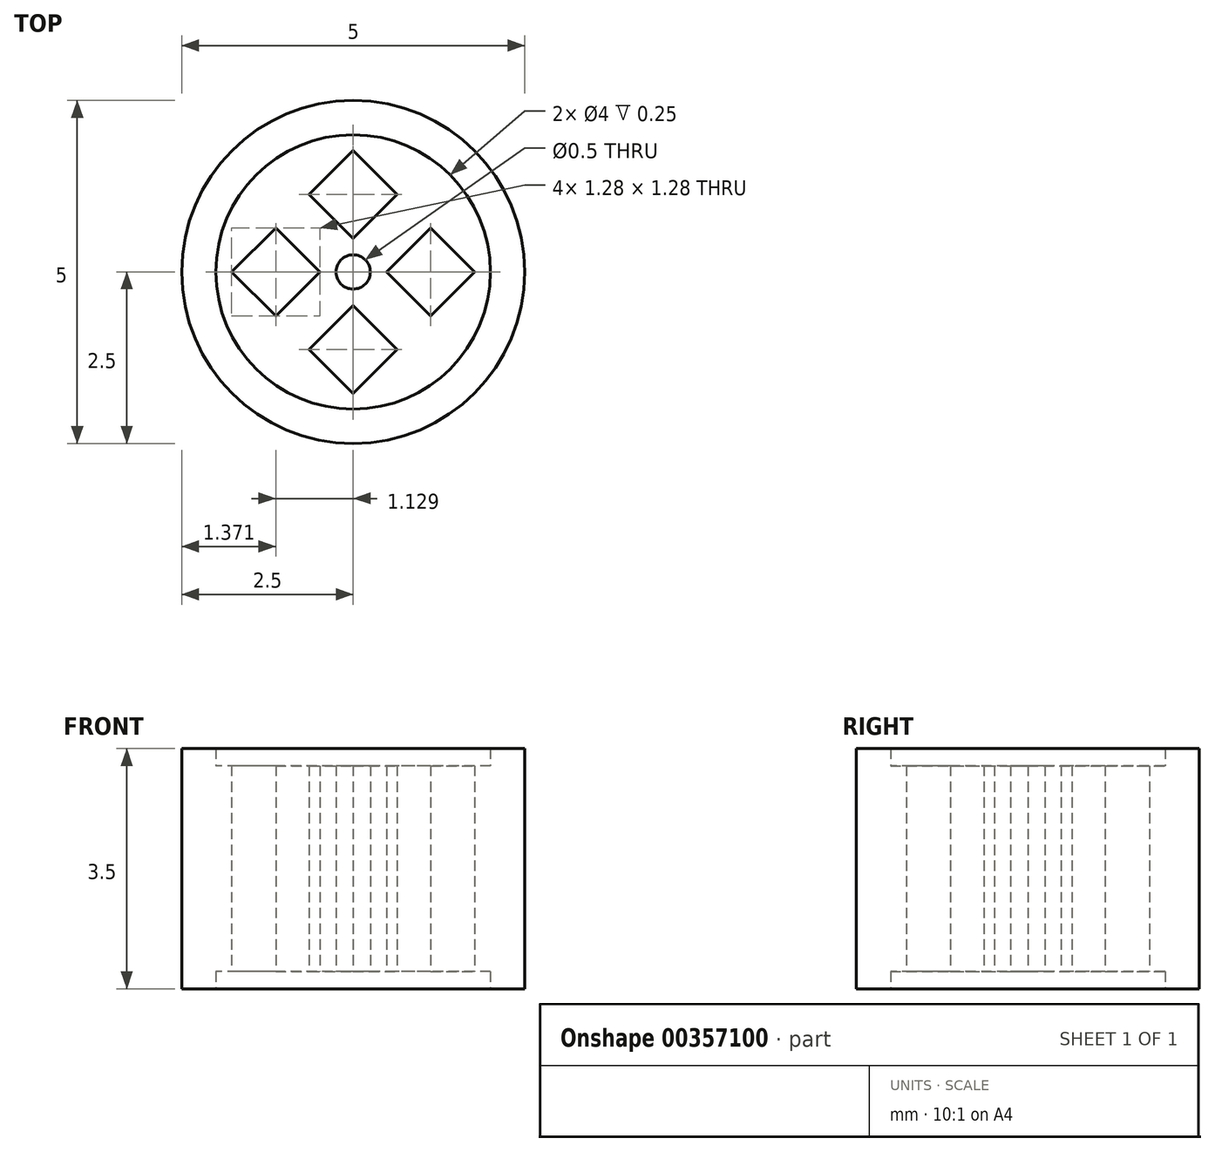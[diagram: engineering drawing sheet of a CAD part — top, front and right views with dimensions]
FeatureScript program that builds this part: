
annotation { "Feature Type Name" : "Feature", "Feature Type Description" : "" }
export const myFeature = defineFeature(function(context is Context, id is Id, definition is map)
    precondition{}
    {
        {
            var Q0;
            Q0=qCreatedBy(makeId("Top.planeOp"),FACE);
            var sketch = newSketch(context, id + "F0", { "sketchPlane" : qUnion([Q0])});
            skCircle(sketch, "E0", {"center": v(0, 0) * mm, "radius": 0.25 * mm});
            skCircle(sketch, "E1", {"center": v(0, 0) * mm, "radius": 2 * mm});
            skCircle(sketch, "E2", {"center": v(0, 0) * mm, "radius": 2.5 * mm});
            skCircle(sketch, "E3.cCircle", {"center": v(0, 1.13) * mm, "radius": 0.45 * mm, "construction": true});
            skLineSegment(sketch, "E3.0", {"start": v(0, 1.77) * mm, "end": v(0.64, 1.13) * mm});
            skLineSegment(sketch, "E3.1", {"start": v(0.64, 1.13) * mm, "end": v(0, 0.49) * mm});
            skLineSegment(sketch, "E3.2", {"start": v(0, 0.49) * mm, "end": v(-0.64, 1.13) * mm});
            skLineSegment(sketch, "E3.3", {"start": v(-0.64, 1.13) * mm, "end": v(0, 1.77) * mm});
            skPoint(sketch, "E3.0.midPoint", {"position": v(0.32, 1.45) * mm});
            skLineSegment(sketch, "E4.1.0", {"start": v(-1.77, 0) * mm, "end": v(-1.13, 0.64) * mm});
            skLineSegment(sketch, "E4.1.1", {"start": v(-1.13, -0.64) * mm, "end": v(-1.77, 0) * mm});
            skLineSegment(sketch, "E4.1.2", {"start": v(-0.49, 0) * mm, "end": v(-1.13, -0.64) * mm});
            skLineSegment(sketch, "E4.1.3", {"start": v(-1.13, 0.64) * mm, "end": v(-0.49, 0) * mm});
            skCircle(sketch, "E4.1.4", {"center": v(-1.13, 0) * mm, "radius": 0.45 * mm, "construction": true});
            skLineSegment(sketch, "E4.2.0", {"start": v(0, -1.77) * mm, "end": v(-0.64, -1.13) * mm});
            skLineSegment(sketch, "E4.2.1", {"start": v(0.64, -1.13) * mm, "end": v(0, -1.77) * mm});
            skLineSegment(sketch, "E4.2.2", {"start": v(0, -0.49) * mm, "end": v(0.64, -1.13) * mm});
            skLineSegment(sketch, "E4.2.3", {"start": v(-0.64, -1.13) * mm, "end": v(0, -0.49) * mm});
            skCircle(sketch, "E4.2.4", {"center": v(0, -1.13) * mm, "radius": 0.45 * mm, "construction": true});
            skLineSegment(sketch, "E4.3.0", {"start": v(1.77, 0) * mm, "end": v(1.13, -0.64) * mm});
            skLineSegment(sketch, "E4.3.1", {"start": v(1.13, 0.64) * mm, "end": v(1.77, 0) * mm});
            skLineSegment(sketch, "E4.3.2", {"start": v(0.49, 0) * mm, "end": v(1.13, 0.64) * mm});
            skLineSegment(sketch, "E4.3.3", {"start": v(1.13, -0.64) * mm, "end": v(0.49, 0) * mm});
            skCircle(sketch, "E4.3.4", {"center": v(1.13, 0) * mm, "radius": 0.45 * mm, "construction": true});
            skSolve(sketch);
        }
        {
            var Q0;
            Q0=makeQuery(id+"F0.imprint","IMPRINT",FACE,{"disambiguationData":[TD([[makeQuery(id+"F0.imprint","IMPRINT",EDGE,{"derivedFrom":sQuery(id+"F0.wireOp",EDGE,"E0")}),-1.0]])]});
            extrude(context, id + "F1", {"entities" : qUnion([Q0]), "endBound" : BoundingType.SYMMETRIC, "depth" : 3 * mm});
        }
        {
            var Q0;
            Q0=makeQuery(id+"F0.imprint","IMPRINT",FACE,{"disambiguationData":[TD([[makeQuery(id+"F0.imprint","IMPRINT",EDGE,{"derivedFrom":sQuery(id+"F0.wireOp",EDGE,"E1")}),-1.0]])]});
            extrude(context, id + "F2", {"entities" : qUnion([Q0]), "operationType" : NewBodyOperationType.ADD, "endBound" : BoundingType.SYMMETRIC, "depth" : 3.5 * mm});
        }
    });
